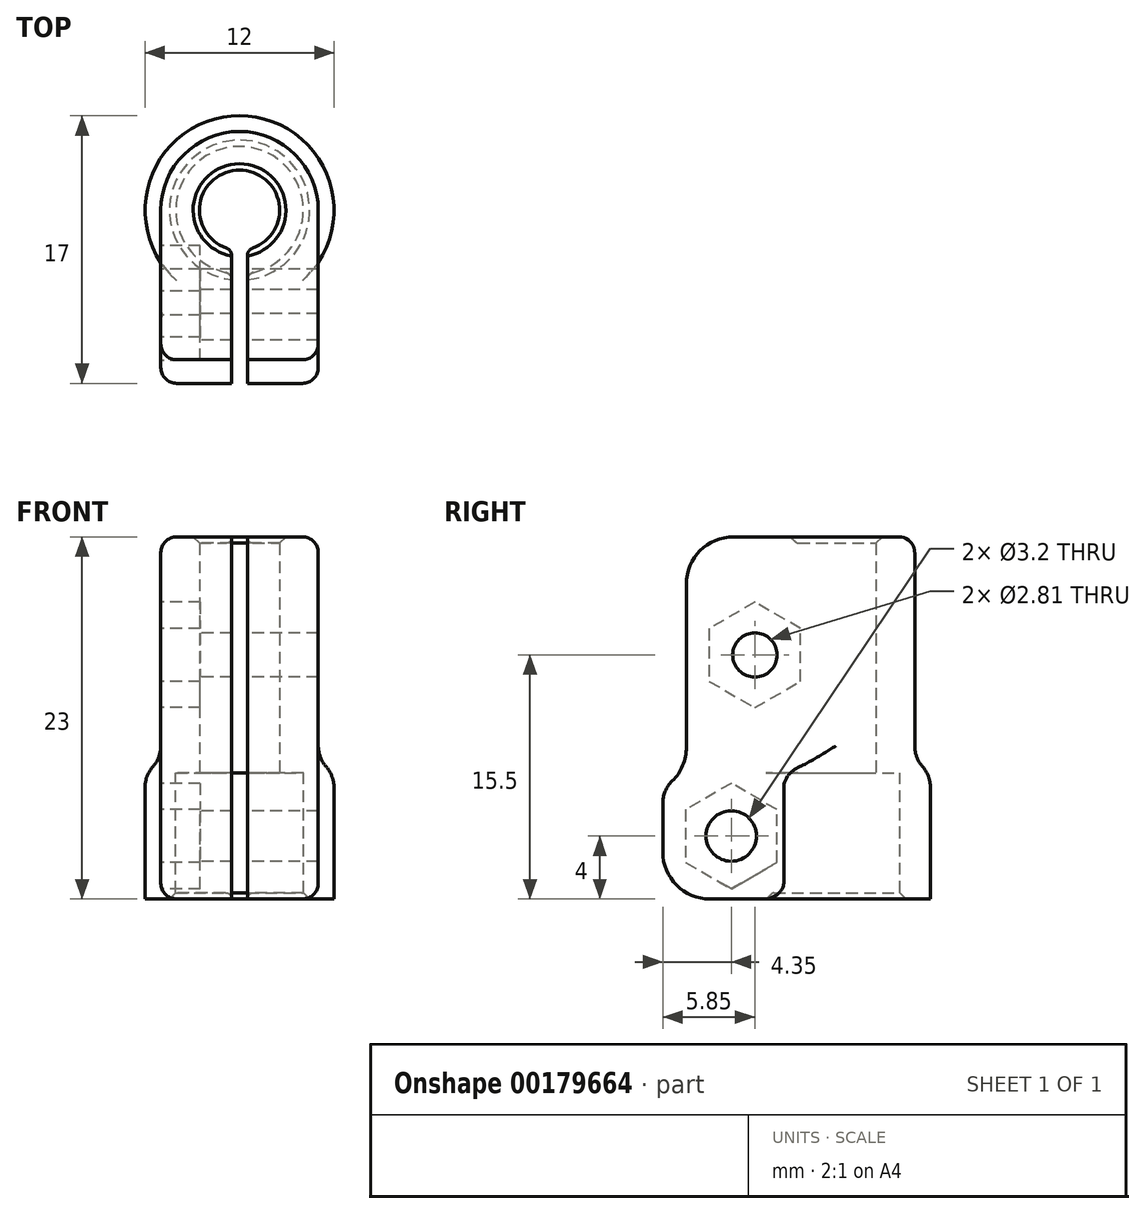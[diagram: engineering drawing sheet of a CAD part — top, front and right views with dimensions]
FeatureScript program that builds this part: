
annotation { "Feature Type Name" : "Feature", "Feature Type Description" : "" }
export const myFeature = defineFeature(function(context is Context, id is Id, definition is map)
    precondition{}
    {
        {
            var Q0;
            Q0=qCreatedBy(makeId("Top.planeOp"),FACE);
            var sketch = newSketch(context, id + "F0", { "sketchPlane" : qUnion([Q0])});
            skCircle(sketch, "E0", {"center": v(0, 0) * mm, "radius": 2.55 * mm});
            skArc(sketch, "E1", {"start": v(5, 0) * mm, "mid": v(0, 5) * mm, "end": v(-5, 0) * mm});
            skLineSegment(sketch, "E2.bottom", {"start": v(-5, -9.5) * mm, "end": v(5, -9.5) * mm});
            skLineSegment(sketch, "E2.left", {"start": v(-5, -9.5) * mm, "end": v(-5, 0) * mm});
            skLineSegment(sketch, "E2.right", {"start": v(5, -9.5) * mm, "end": v(5, 0) * mm});
            skPoint(sketch, "E3", {"position": v(0, -9.5) * mm});
            skLineSegment(sketch, "E4", {"start": v(5, -5.15) * mm, "end": v(-5, -5.15) * mm, "construction": true});
            skSolve(sketch);
        }
        {
            var Q0;
            Q0=qSketchRegion(id+"F0",true);
            extrude(context, id + "F1", {"entities" : qUnion([Q0]), "depth" : 15 * mm});
        }
        {
            var Q0;
            Q0=makeQuery(id+"F1.opExtrude","SWEPT_FACE",FACE,{"disambiguationData":[OSD([sQuery(id+"F0.wireOp",EDGE,"E2.left")])]});
            var sketch = newSketch(context, id + "F2", { "sketchPlane" : qUnion([Q0])});
            skLineSegment(sketch, "E5.0.0", {"start": v(0, 0) * mm, "end": v(9.5, 0) * mm, "construction": true});
            skLineSegment(sketch, "E5.0.1", {"start": v(9.5, 0) * mm, "end": v(9.5, 15) * mm, "construction": true});
            skLineSegment(sketch, "E5.0.2", {"start": v(9.5, 15) * mm, "end": v(0, 15) * mm, "construction": true});
            skLineSegment(sketch, "E5.0.3", {"start": v(0, 15) * mm, "end": v(0, 0) * mm, "construction": true});
            skLineSegment(sketch, "E6.0", {"start": v(-2.55, 0) * mm, "end": v(2.55, 0) * mm, "construction": true});
            skCircle(sketch, "E7", {"center": v(5.15, 7.5) * mm, "radius": 1.4 * mm});
            skLineSegment(sketch, "E8", {"start": v(2.55, 0) * mm, "end": v(2.55, 15) * mm, "construction": true});
            skLineSegment(sketch, "E9", {"start": v(9.5, 7.5) * mm, "end": v(2.55, 7.5) * mm, "construction": true});
            skSolve(sketch);
        }
        {
            var Q0;
            Q0=makeQuery(id+"F2.imprint","IMPRINT",FACE,{"disambiguationData":[TD([[makeQuery(id+"F2.imprint","IMPRINT",EDGE,{"derivedFrom":sQuery(id+"F2.wireOp",EDGE,"E7")}),1.0]])]});
            var Q1;
            Q1=sQuery(id+"F2.wireOp",EDGE,"E7");
            extrude(context, id + "F3", {"entities" : qUnion([Q0]), "operationType" : NewBodyOperationType.REMOVE, "surfaceEntities" : qUnion([Q1]), "endBound" : BoundingType.THROUGH_ALL, "oppositeDirection" : true, "depth" : 25 * mm});
        }
        {
            var Q0;
            Q0=makeQuery(id+"F1.opExtrude","SWEPT_FACE",FACE,{"disambiguationData":[OSD([sQuery(id+"F0.wireOp",EDGE,"E2.left")])]});
            var sketch = newSketch(context, id + "F4", { "sketchPlane" : qUnion([Q0])});
            skCircle(sketch, "E10.0", {"center": v(5.15, 7.5) * mm, "radius": 1.4 * mm});
            skCircle(sketch, "E11.cCircle", {"center": v(5.15, 7.5) * mm, "radius": 3.35 * mm, "construction": true});
            skLineSegment(sketch, "E11.0", {"start": v(2.25, 5.82) * mm, "end": v(2.25, 9.17) * mm});
            skLineSegment(sketch, "E11.1", {"start": v(2.25, 9.17) * mm, "end": v(5.15, 10.85) * mm});
            skLineSegment(sketch, "E11.2", {"start": v(5.15, 10.85) * mm, "end": v(8.05, 9.18) * mm});
            skLineSegment(sketch, "E11.3", {"start": v(8.05, 9.17) * mm, "end": v(8.05, 5.83) * mm});
            skLineSegment(sketch, "E11.4", {"start": v(8.05, 5.83) * mm, "end": v(5.15, 4.15) * mm});
            skLineSegment(sketch, "E11.5", {"start": v(5.15, 4.15) * mm, "end": v(2.25, 5.82) * mm});
            skSolve(sketch);
        }
        {
            var Q0;
            Q0=qSketchRegion(id+"F4",true);
            extrude(context, id + "F5", {"entities" : qUnion([Q0]), "operationType" : NewBodyOperationType.REMOVE, "oppositeDirection" : true, "depth" : 2.5 * mm});
        }
        {
            var Q0;
            Q0=makeQuery(id+"F1.opExtrude","CAP_FACE",FACE,{"disambiguationData":[OSD([sQuery(id+"F0.wireOp",EDGE,"E0"),sQuery(id+"F0.wireOp",EDGE,"E1"),sQuery(id+"F0.wireOp",EDGE,"E2.bottom"),sQuery(id+"F0.wireOp",EDGE,"E2.left"),sQuery(id+"F0.wireOp",EDGE,"E2.right")])],"isStart":true});
            var sketch = newSketch(context, id + "F6", { "sketchPlane" : qUnion([Q0])});
            skLineSegment(sketch, "E12.0", {"start": v(-5, 9.5) * mm, "end": v(5, 9.5) * mm, "construction": true});
            skCircle(sketch, "E13.0", {"center": v(0, 0) * mm, "radius": 2.55 * mm, "construction": true});
            skCircle(sketch, "E14", {"center": v(0, 0) * mm, "radius": 4.05 * mm});
            skArc(sketch, "E15", {"start": v(-5, 3.32) * mm, "mid": v(0, -6) * mm, "end": v(5, 3.32) * mm});
            skLineSegment(sketch, "E16", {"start": v(-5, 3.32) * mm, "end": v(-5, 11) * mm});
            skLineSegment(sketch, "E17", {"start": v(-5, 11) * mm, "end": v(5, 11) * mm});
            skLineSegment(sketch, "E18", {"start": v(5, 11) * mm, "end": v(5, 3.32) * mm});
            skLineSegment(sketch, "E19", {"start": v(-5, 6.65) * mm, "end": v(5, 6.65) * mm, "construction": true});
            skSolve(sketch);
        }
        {
            var Q0;
            Q0=qSketchRegion(id+"F6",true);
            extrude(context, id + "F7", {"entities" : qUnion([Q0]), "operationType" : NewBodyOperationType.ADD, "depth" : 8 * mm});
        }
        {
            var Q0;
            Q0=makeQuery(id+"F7.boolean.opBoolean","MERGE",FACE,{"derivedFrom":[makeQuery(id+"F1.opExtrude","SWEPT_FACE",FACE,{"disambiguationData":[OSD([sQuery(id+"F0.wireOp",EDGE,"E2.left")])]}),makeQuery(id+"F7.opExtrude","SWEPT_FACE",FACE,{"disambiguationData":[OSD([sQuery(id+"F6.wireOp",EDGE,"E16")])]})]});
            var sketch = newSketch(context, id + "F8", { "sketchPlane" : qUnion([Q0])});
            skLineSegment(sketch, "E20.0", {"start": v(4.05, -8) * mm, "end": v(-4.05, -8) * mm, "construction": true});
            skCircle(sketch, "E21", {"center": v(6.65, -4) * mm, "radius": 1.6 * mm});
            skLineSegment(sketch, "E22", {"start": v(3.32, -4) * mm, "end": v(11, -4) * mm, "construction": true});
            skSolve(sketch);
        }
        {
            var Q0;
            Q0=qSketchRegion(id+"F8",true);
            extrude(context, id + "F9", {"entities" : qUnion([Q0]), "operationType" : NewBodyOperationType.REMOVE, "endBound" : BoundingType.THROUGH_ALL, "oppositeDirection" : true, "depth" : 25 * mm});
        }
        {
            var Q0;
            Q0=makeQuery(id+"F7.boolean.opBoolean","MERGE",FACE,{"derivedFrom":[makeQuery(id+"F1.opExtrude","SWEPT_FACE",FACE,{"disambiguationData":[OSD([sQuery(id+"F0.wireOp",EDGE,"E2.left")])]}),makeQuery(id+"F7.opExtrude","SWEPT_FACE",FACE,{"disambiguationData":[OSD([sQuery(id+"F6.wireOp",EDGE,"E16")])]})]});
            var sketch = newSketch(context, id + "F10", { "sketchPlane" : qUnion([Q0])});
            skCircle(sketch, "E23.cCircle", {"center": v(6.65, -4) * mm, "radius": 3.35 * mm, "construction": true});
            skLineSegment(sketch, "E23.0", {"start": v(3.75, -5.67) * mm, "end": v(3.75, -2.33) * mm});
            skLineSegment(sketch, "E23.1", {"start": v(3.75, -2.33) * mm, "end": v(6.65, -0.65) * mm});
            skLineSegment(sketch, "E23.2", {"start": v(6.65, -0.65) * mm, "end": v(9.55, -2.33) * mm});
            skLineSegment(sketch, "E23.3", {"start": v(9.55, -2.33) * mm, "end": v(9.55, -5.67) * mm});
            skLineSegment(sketch, "E23.4", {"start": v(9.55, -5.68) * mm, "end": v(6.65, -7.35) * mm});
            skLineSegment(sketch, "E23.5", {"start": v(6.65, -7.35) * mm, "end": v(3.75, -5.68) * mm});
            skSolve(sketch);
        }
        {
            var Q0;
            Q0=qSketchRegion(id+"F10",true);
            extrude(context, id + "F11", {"entities" : qUnion([Q0]), "operationType" : NewBodyOperationType.REMOVE, "oppositeDirection" : true, "depth" : 2.5 * mm});
        }
        {
            var Q0;
            Q0=makeQuery(id+"F1.opExtrude","CAP_EDGE",EDGE,{"disambiguationData":[OSD([sQuery(id+"F0.wireOp",EDGE,"E1")])],"isStart":true});
            fillet(context, id + "F12", {"entities" : qUnion([Q0]), "radius" : 2 * mm, "tangentPropagation" : true, "allowEdgeOverflow" : false});
        }
        {
            var Q0;
            Q0=makeQuery(id+"F12.opFillet","BLEND_EDGE",EDGE,{"blendedFrom":[makeQuery(id+"F1.opExtrude","CAP_EDGE",EDGE,{"disambiguationData":[OSD([sQuery(id+"F0.wireOp",EDGE,"E1")])],"isStart":true}),makeQuery(id+"F7.opExtrude","SWEPT_FACE",FACE,{"disambiguationData":[OSD([sQuery(id+"F6.wireOp",EDGE,"E15")])]})],"blendedInto":[makeQuery(id+"F7.opExtrude","SWEPT_FACE",FACE,{"disambiguationData":[OSD([sQuery(id+"F6.wireOp",EDGE,"E15")])]})]});
            fillet(context, id + "F13", {"entities" : qUnion([Q0]), "radius" : 2 * mm, "tangentPropagation" : true, "allowEdgeOverflow" : false});
        }
        {
            var Q0;
            Q0=makeQuery(id+"F7.opExtrude","CAP_EDGE",EDGE,{"disambiguationData":[OSD([sQuery(id+"F6.wireOp",EDGE,"E17")])],"isStart":true});
            fillet(context, id + "F14", {"entities" : qUnion([Q0]), "radius" : 2 * mm, "tangentPropagation" : true, "allowEdgeOverflow" : false});
        }
        {
            var Q0;
            Q0=makeQuery(id+"F14.opFillet","BLEND_EDGE",EDGE,{"blendedFrom":[makeQuery(id+"F7.opExtrude","CAP_EDGE",EDGE,{"disambiguationData":[OSD([sQuery(id+"F6.wireOp",EDGE,"E17")])],"isStart":true}),makeQuery(id+"F1.opExtrude","SWEPT_FACE",FACE,{"disambiguationData":[OSD([sQuery(id+"F0.wireOp",EDGE,"E2.bottom")])]})],"blendedInto":[makeQuery(id+"F1.opExtrude","SWEPT_FACE",FACE,{"disambiguationData":[OSD([sQuery(id+"F0.wireOp",EDGE,"E2.bottom")])]})]});
            fillet(context, id + "F15", {"entities" : qUnion([Q0]), "radius" : 3 * mm, "tangentPropagation" : true, "allowEdgeOverflow" : false});
        }
        {
            var Q0;
            Q0=makeQuery(id+"F1.opExtrude","CAP_EDGE",EDGE,{"disambiguationData":[OSD([sQuery(id+"F0.wireOp",EDGE,"E2.bottom")])],"isStart":false});
            var Q1;
            Q1=makeQuery(id+"F7.opExtrude","CAP_EDGE",EDGE,{"disambiguationData":[OSD([sQuery(id+"F6.wireOp",EDGE,"E17")])],"isStart":false});
            fillet(context, id + "F16", {"entities" : qUnion([Q0, Q1]), "radius" : 3 * mm, "tangentPropagation" : true, "allowEdgeOverflow" : false});
        }
        {
            var Q0;
            Q0=makeQuery(id+"F7.opExtrude","CAP_EDGE",EDGE,{"disambiguationData":[OSD([sQuery(id+"F6.wireOp",EDGE,"E14")])],"isStart":false});
            var Q1;
            Q1=makeQuery(id+"F1.opExtrude","CAP_EDGE",EDGE,{"disambiguationData":[OSD([sQuery(id+"F0.wireOp",EDGE,"E0")])],"isStart":false});
            chamfer(context, id + "F17", {"entities" : qUnion([Q0, Q1]), "width" : 0.4 * mm, "tangentPropagation" : true});
        }
        {
            var Q0;
            Q0=makeQuery(id+"F1.opExtrude","CAP_FACE",FACE,{"disambiguationData":[OSD([sQuery(id+"F0.wireOp",EDGE,"E0"),sQuery(id+"F0.wireOp",EDGE,"E1"),sQuery(id+"F0.wireOp",EDGE,"E2.bottom"),sQuery(id+"F0.wireOp",EDGE,"E2.left"),sQuery(id+"F0.wireOp",EDGE,"E2.right")])],"isStart":false});
            var sketch = newSketch(context, id + "F18", { "sketchPlane" : qUnion([Q0])});
            skLineSegment(sketch, "E24.bottom", {"start": v(-0.5, 0) * mm, "end": v(0.5, 0) * mm});
            skLineSegment(sketch, "E24.top", {"start": v(-0.5, -14.1) * mm, "end": v(0.5, -14.1) * mm});
            skLineSegment(sketch, "E24.left", {"start": v(-0.5, 0) * mm, "end": v(-0.5, -14.1) * mm});
            skLineSegment(sketch, "E24.right", {"start": v(0.5, 0) * mm, "end": v(0.5, -14.1) * mm});
            skSolve(sketch);
        }
        {
            var Q0;
            Q0=qSketchRegion(id+"F18",true);
            extrude(context, id + "F19", {"entities" : qUnion([Q0]), "operationType" : NewBodyOperationType.REMOVE, "endBound" : BoundingType.THROUGH_ALL, "oppositeDirection" : true, "depth" : 25 * mm});
        }
        {
            var Q0;
            Q0=makeQuery(id+"F1.opExtrude","CAP_EDGE",EDGE,{"disambiguationData":[OSD([sQuery(id+"F0.wireOp",EDGE,"E1")])],"isStart":false});
            fillet(context, id + "F20", {"entities" : qUnion([Q0]), "radius" : 1 * mm, "tangentPropagation" : true, "allowEdgeOverflow" : false});
        }
        {
            var Q0;
            Q0=makeQuery(id+"F19.boolean.opBoolean","INTERSECT",EDGE,{"derivedFrom":[makeQuery(id+"F1.opExtrude","SWEPT_FACE",FACE,{"disambiguationData":[OSD([sQuery(id+"F0.wireOp",EDGE,"E0")])]}),makeQuery(id+"F19.opExtrude","SWEPT_FACE",FACE,{"disambiguationData":[OSD([sQuery(id+"F18.wireOp",EDGE,"E24.left")])]})]});
            var Q1;
            Q1=makeQuery(id+"F19.boolean.opBoolean","INTERSECT",EDGE,{"derivedFrom":[makeQuery(id+"F1.opExtrude","SWEPT_FACE",FACE,{"disambiguationData":[OSD([sQuery(id+"F0.wireOp",EDGE,"E0")])]}),makeQuery(id+"F19.opExtrude","SWEPT_FACE",FACE,{"disambiguationData":[OSD([sQuery(id+"F18.wireOp",EDGE,"E24.right")])]})]});
            var Q2;
            Q2=makeQuery(id+"F19.boolean.opBoolean","INTERSECT",EDGE,{"derivedFrom":[makeQuery(id+"F7.opExtrude","SWEPT_FACE",FACE,{"disambiguationData":[OSD([sQuery(id+"F6.wireOp",EDGE,"E14")])]}),makeQuery(id+"F19.opExtrude","SWEPT_FACE",FACE,{"disambiguationData":[OSD([sQuery(id+"F18.wireOp",EDGE,"E24.left")])]})]});
            var Q3;
            Q3=makeQuery(id+"F19.boolean.opBoolean","INTERSECT",EDGE,{"derivedFrom":[makeQuery(id+"F7.opExtrude","SWEPT_FACE",FACE,{"disambiguationData":[OSD([sQuery(id+"F6.wireOp",EDGE,"E14")])]}),makeQuery(id+"F19.opExtrude","SWEPT_FACE",FACE,{"disambiguationData":[OSD([sQuery(id+"F18.wireOp",EDGE,"E24.right")])]})]});
            fillet(context, id + "F21", {"entities" : qUnion([Q0, Q1, Q2, Q3]), "radius" : 0.5 * mm, "tangentPropagation" : true, "allowEdgeOverflow" : false});
        }
    });
